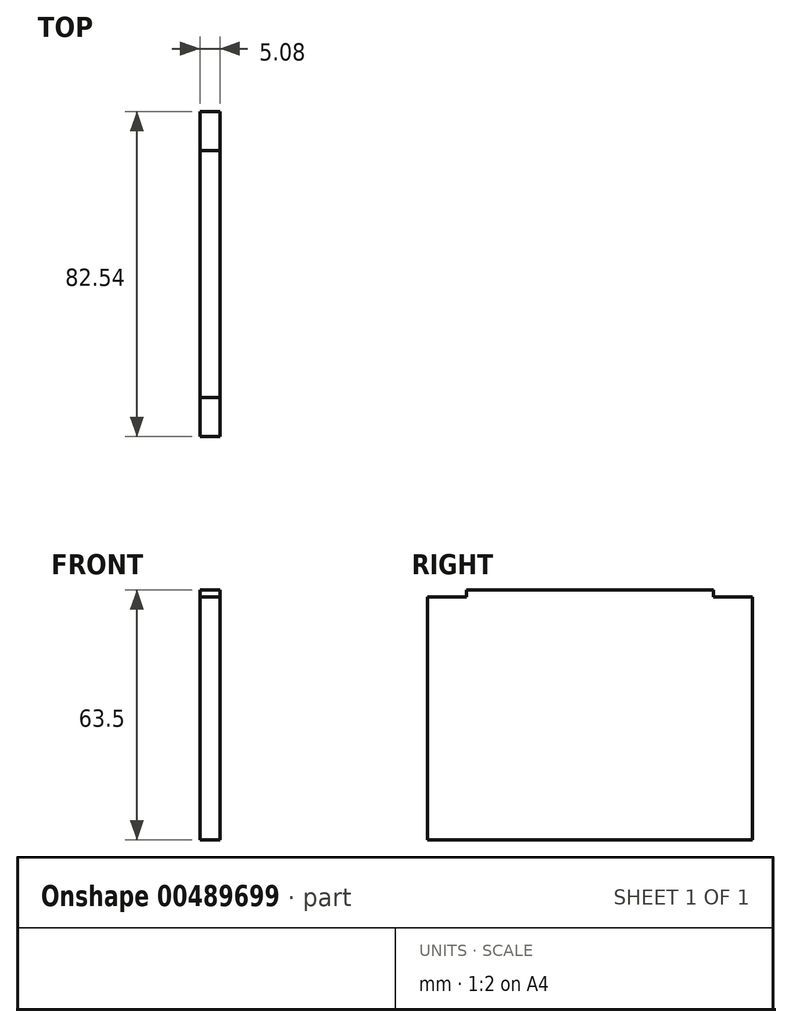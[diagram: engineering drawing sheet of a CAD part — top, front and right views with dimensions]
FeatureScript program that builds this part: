
annotation { "Feature Type Name" : "Feature", "Feature Type Description" : "" }
export const myFeature = defineFeature(function(context is Context, id is Id, definition is map)
    precondition{}
    {
        {
            var Q0;
            Q0=qCreatedBy(makeId("Right.planeOp"),FACE);
            var sketch = newSketch(context, id + "F0", { "sketchPlane" : qUnion([Q0])});
            skLineSegment(sketch, "E0.bottom", {"start": v(41.28, -31.75) * mm, "end": v(-41.28, -31.75) * mm});
            skLineSegment(sketch, "E0.top", {"start": v(31.37, 31.75) * mm, "end": v(-31.37, 31.75) * mm});
            skLineSegment(sketch, "E0.left", {"start": v(41.28, -31.75) * mm, "end": v(41.28, 29.97) * mm});
            skLineSegment(sketch, "E0.right", {"start": v(-41.28, -31.75) * mm, "end": v(-41.28, 29.97) * mm});
            skPoint(sketch, "E0.middle", {"position": v(0, 0) * mm});
            skLineSegment(sketch, "E1", {"start": v(-31.37, 31.75) * mm, "end": v(-31.37, 29.97) * mm});
            skLineSegment(sketch, "E2", {"start": v(-31.37, 29.97) * mm, "end": v(-41.28, 29.97) * mm});
            skLineSegment(sketch, "E3", {"start": v(41.28, 29.97) * mm, "end": v(31.37, 29.97) * mm});
            skPoint(sketch, "E4.start.orphan", {"position": v(31.37, 31.75) * mm});
            skPoint(sketch, "E5.orphan", {"position": v(41.28, 31.75) * mm});
            skPoint(sketch, "E6.orphan", {"position": v(-41.28, 31.75) * mm});
            skLineSegment(sketch, "E7", {"start": v(31.37, 31.75) * mm, "end": v(31.37, 29.97) * mm});
            skSolve(sketch);
        }
        {
            var Q0;
            Q0 = qSketchRegion(id + "F0", true);
            extrude(context, id + "F1", {"entities" : qUnion([Q0]), "depth" : 5.08 * mm});
        }
    });
